# Revit family: Shower-Bath_and_Shower-KOHLER-Alteo-K-TS45104
name_source: partatom
category: Plumbing Fixtures
revit_build: Autodesk Revit 2015 (Build: 20140606_1530(x64)
units: mm (PartAtom-declared; Revit-internal decimal feet)

## types (5) — shared parameters
ADA Compliant = No
Assembly Code = D2010700
CW Connection = No
Date Modified = 09/07/2018
Default Elevation = 42"
Description = Rite-Temp bath and shower trim set, valve not included
HW Connection = Yes
Height = 6 7/16"
Length = 6 3/8"
Manufacturer = KOHLER Co.
MasterFormat 1995 = 15410
MasterFormat 2004 = 22.41.23
Material = Premium Material Construction
Panel Thickness = 0"
Pressure = 80.00 psi
Product Documentation Link = http://www.us.kohler.com
Product Name = Alteo
Product Page URL = http://www.us.kohler.com
Tempered Water Inlet 1 = Tempered Water Inlet 1
Tempered Water Inlet 2 = Tempered Water Inlet 2
URL = https://www.us.kohler.com
Vent Connection = No
Waste Connection = No
Waste Water Outlet = Waste Water Outlet
Width = 6 7/16"

## per-type parameters (varying)
| type | Finish | Flow Rate | Model | Type |
| 2.5 GPM, CP-Polished Chrome | Kohler-Metal-CP-Polished_Chrome | 3 GPM | K-TS45104-4-CP | 1 |
| 2.5 GPM, BN-Vibrant Brushed Nickel | Kohler-Metal-BN-Vibrant_Brushed_Nickel | 3 GPM | K-TS45104-4-BN | 2 |
| 2.5 GPM, 2BZ-Oil Rubbed Bronze | Kohler-Metal-2BZ-Oil_Rubbed_Bronze | 3 GPM | K-TS45104-4-2BZ | 3 |
| 2 GPM, CP-Polished Chrome | Kohler-Metal-CP-Polished_Chrome | 2 GPM | K-TS45104-4E-CP | 4 |
| 2 GPM, BN-Vibrant Brushed Nickel | Kohler-Metal-BN-Vibrant_Brushed_Nickel | 2 GPM | K-TS45104-4E-BN | 5 |

## geometry (parser evidence)
native form markers: Sweep x9
no freeform markers — native parametric forms only
